FCSTD DOCUMENT  (FreeCAD 1.0R39319 (Git))
Label: three_wires_ribbon
License: All rights reserved
LicenseURL: http://en.wikipedia.org/wiki/All_rights_reserved
objects: Part::Part2DObjectPython×7, App::FeaturePython×7, App::DocumentObjectGroup×4, App::DocumentObjectGroupPython×3, Spreadsheet::Sheet×1
note: 7 computed .brp shape members not serialized (recipe doc carries the construction recipe); baked Part::Feature solids carry a one-line shape summary decoded from their .brp

FEATURE [Part::Part2DObjectPython] Circle002  label="Dielectric_0"  # Draft 2D object (typed FeaturePython)
  Area = 0.620717
  FirstAngle = 0
  LastAngle = 0
  MakeFace = true
  Radius = 0.4445
  expr: Radius = Spreadsheet.rw + Spreadsheet.th
FEATURE [Spreadsheet::Sheet] Spreadsheet
  cells = A2='Wire radius; B2(rw)==7.5 mil; A3='Dielectric thickness; B3(th)==10 mil; A4='Distance between wires; B4(d)==50 mil; A5='Outer domain radius; B5(rd)==150 mm; A6='Dielectric permittivity; B6(eps_r)=3.5
FEATURE [Part::Part2DObjectPython] Circle001  label="Conductor_000"  # Draft 2D object (typed FeaturePython)
  Area = 0.114009
  FirstAngle = 0
  LastAngle = 0
  MakeFace = true
  Radius = 0.1905
  expr: Radius = Spreadsheet.rw
FEATURE [App::DocumentObjectGroup] Group  label="solid_wire_000"
  Group = -> [Circle001,Circle002]
FEATURE [Part::Part2DObjectPython] Circle003  label="Conductor_001"  # Draft 2D object (typed FeaturePython)
  Area = 0.114009
  FirstAngle = 0
  LastAngle = 0
  MakeFace = true
  Placement = pos=(1.27,0,0) rot=(0,0,1;0rad)
  Radius = 0.1905
  expr: .Placement.Base.x = Spreadsheet.d
  expr: Radius = Spreadsheet.rw
FEATURE [Part::Part2DObjectPython] Circle004  label="Dielectric_001"  # Draft 2D object (typed FeaturePython)
  Area = 0.620717
  FirstAngle = 0
  LastAngle = 0
  MakeFace = true
  Placement = pos=(1.27,0,0) rot=(0,0,1;0rad)
  Radius = 0.4445
  expr: .Placement.Base.x = Spreadsheet.d
  expr: Radius = Spreadsheet.rw + Spreadsheet.th
FEATURE [App::DocumentObjectGroup] Group006  label="solid_wire_001"
  Group = -> [Circle003,Circle004]
FEATURE [Part::Part2DObjectPython] Circle005  label="Conductor_002"  # Draft 2D object (typed FeaturePython)
  Area = 0.114009
  FirstAngle = 0
  LastAngle = 0
  MakeFace = true
  Placement = pos=(2.54,0,0) rot=(0,0,1;0rad)
  Radius = 0.1905
  expr: .Placement.Base.x = 2 * Spreadsheet.d
  expr: Radius = Spreadsheet.rw
FEATURE [Part::Part2DObjectPython] Circle006  label="Dielectric_002"  # Draft 2D object (typed FeaturePython)
  Area = 0.620717
  FirstAngle = 0
  LastAngle = 0
  MakeFace = true
  Placement = pos=(2.54,0,0) rot=(0,0,1;0rad)
  Radius = 0.4445
  expr: .Placement.Base.x = 2 * Spreadsheet.d
  expr: Radius = Spreadsheet.rw + Spreadsheet.th
FEATURE [App::DocumentObjectGroup] Group007  label="solid_wire_002"
  Group = -> [Circle005,Circle006]
FEATURE [App::FeaturePython] Dimension  # Draft dimension (typed FeaturePython)
  Diameter = false
  Dimline = (0.252552,-0.901386,0)
  Direction = (0,0,0)
  Distance = 1.27
  End = (1.27,1e-16,0)
  Normal = (0,0,1)
  Start = (0,0,0)
FEATURE [App::FeaturePython] Dimension002  # Draft dimension (typed FeaturePython)
  Diameter = true
  Dimline = (1.75225,0.559104,0)
  Direction = (0,0,0)
  Distance = 0.889
  End = (1.56032,0.336589,0)
  LinkedGeometry = -> [Circle004]
  Normal = (0,0,1)
  Start = (0.979676,-0.336589,0)
  Support = -> Circle004
FEATURE [App::FeaturePython] Dimension003  # Draft dimension (typed FeaturePython)
  Diameter = true
  Dimline = (0.4,0.4,0)
  Direction = (0,0,0)
  Distance = 0.381
  End = (0.134704,0.134704,0)
  LinkedGeometry = -> [Circle001]
  Normal = (0,0,1)
  Start = (-0.134704,-0.134704,0)
  Support = -> Circle001
FEATURE [App::FeaturePython] Text002  # WARN: FeaturePython — macro-defined, semantics opaque (R4)
  Placement = pos=(-0.563454,0.608429,0) rot=(0,0,1;0rad)
  Text = Conductor 0
FEATURE [App::FeaturePython] Text003  # WARN: FeaturePython — macro-defined, semantics opaque (R4)
  Placement = pos=(0.74166,0.60074,0) rot=(0,0,1;0rad)
  Text = Conductor 1
FEATURE [App::FeaturePython] Text004  # WARN: FeaturePython — macro-defined, semantics opaque (R4)
  Placement = pos=(1.98424,0.611182,0) rot=(0,0,1;0rad)
  Text = Conductor 2
FEATURE [App::FeaturePython] Text  # WARN: FeaturePython — macro-defined, semantics opaque (R4)
  Placement = pos=(2.87662,-0.483203,0) rot=(0,0,1;0rad)
  Text = Permittivity = 3.5
FEATURE [Part::Part2DObjectPython] Circle  label="OpenBoundary_0"  # Draft 2D object (typed FeaturePython)
  Area = 70685.8
  FirstAngle = 0
  LastAngle = 0
  MakeFace = true
  Placement = pos=(1.27,1e-16,0) rot=(0,0,1;0rad)
  Radius = 150
  expr: .Placement.Base.x = Spreadsheet.d
  expr: Radius = Spreadsheet.rd
FEATURE [App::DocumentObjectGroup] Group005  label="Domain_0"
  Group = -> [Group,Group006,Group007,Circle]
FEATURE [App::DocumentObjectGroupPython] MaterialGroup  label="Materials"  # scripted group (container) (typed FeaturePython)
FEATURE [App::DocumentObjectGroupPython] CaseStudy  label="Model"  # scripted group (container) (typed FeaturePython)
  Group = -> [Group005]
FEATURE [App::DocumentObjectGroupPython] CrossSection  label="Cross-Section"  # scripted group (container) (typed FeaturePython)
  Group = -> [MaterialGroup,CaseStudy]
